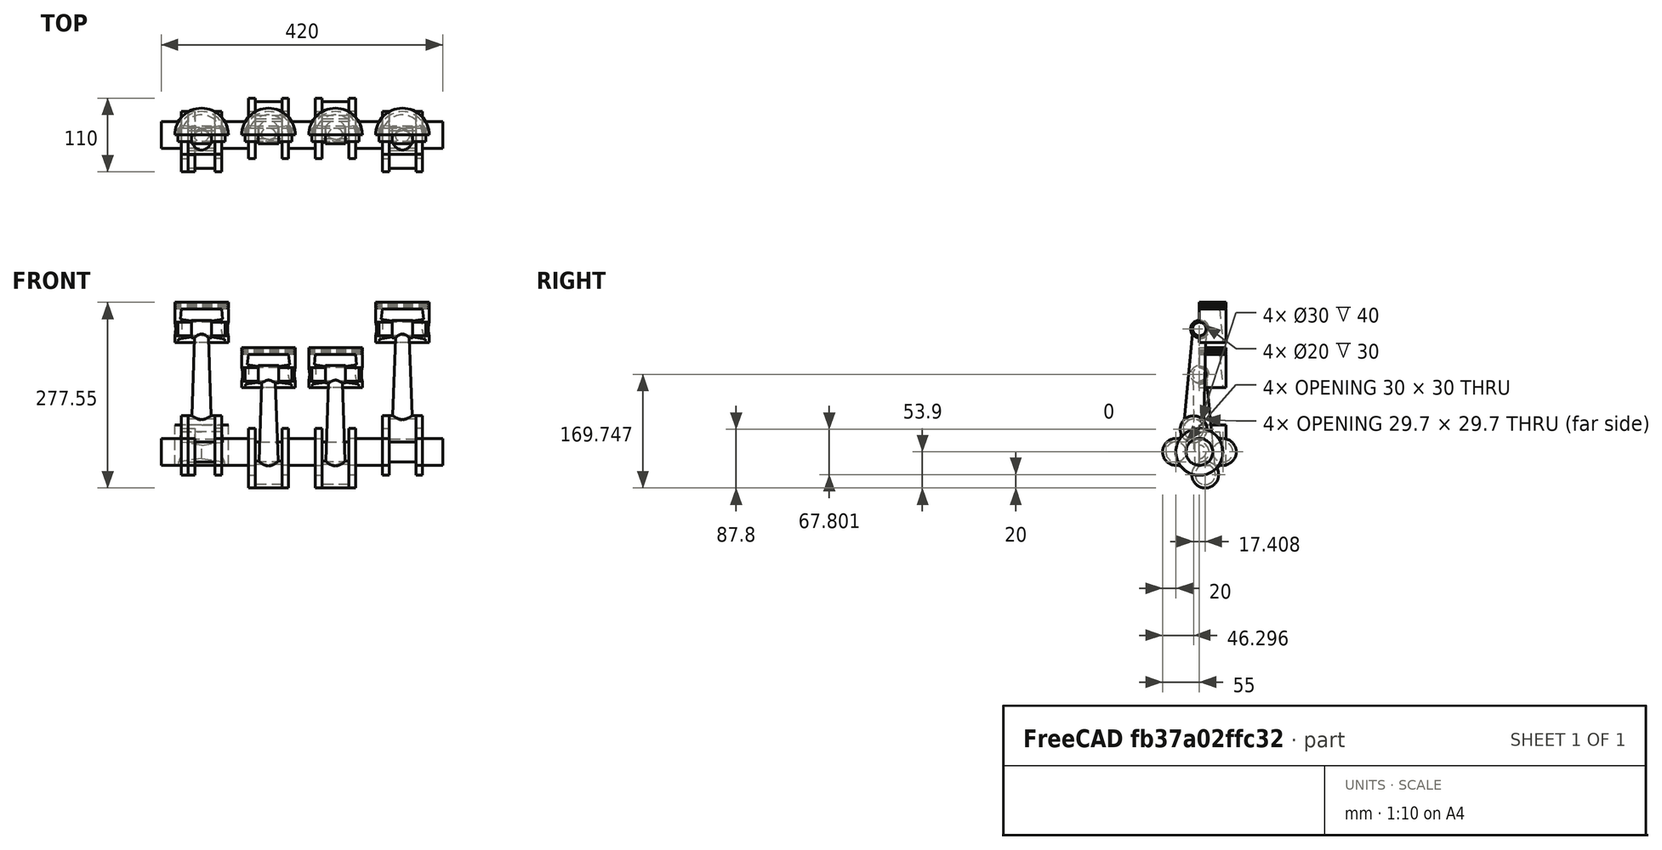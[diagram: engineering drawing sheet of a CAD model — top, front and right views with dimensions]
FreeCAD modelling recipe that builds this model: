
FCSTD DOCUMENT  (FreeCAD 0.18R16093 +53 (Git))
Label: 198 - ENGINE ANIMATION
License: All rights reserved
LicenseURL: http://en.wikipedia.org/wiki/All_rights_reserved
objects: Part::Cylinder×33, Part::Feature×20, Part::Cut×17, Part::Compound×12, App::DocumentObjectGroupPython×10, Part::MultiFuse×9, Part::Cone×6, Part::FeaturePython×4, Part::Fillet×1
note: 102 computed .brp shape members not serialized (recipe doc carries the construction recipe); baked Part::Feature solids carry a one-line shape summary decoded from their .brp

FEATURE [Part::Cylinder] Cylinder
  Angle = 180
  AttacherType = Attacher::AttachEngine3D
  Height = 60
  Placement = pos=(0,0,-20) rot=(0,0,1;0rad)
  Radius = 40
FEATURE [Part::Cone] Cone
  Angle = 360
  AttacherType = Attacher::AttachEngine3D
  Height = 50
  Placement = pos=(0,0,-20) rot=(0,0,1;0rad)
  Radius1 = 35
  Radius2 = 30
FEATURE [Part::Cut] Cut
  Base = -> Cylinder
  Tool = -> Cone
FEATURE [Part::Cone] Cone001
  Angle = 180
  AttacherType = Attacher::AttachEngine3D
  Height = 35
  Placement = pos=(0,0,0) rot=(0,-1,0;1.5708rad)
  Radius1 = 10
  Radius2 = 15
FEATURE [Part::Feature] Cone001001  label="Cone002"
  Placement = pos=(0,0,0) rot=(0,1,0;1.5708rad)
  shape: bbox 35 x 15 x 30 mm, 5 faces (baked)
FEATURE [Part::MultiFuse] Fusion
  Shapes = -> [Cone001001,Cone001,Cut]
FEATURE [Part::Feature] Fusion001
  shape: bbox 80 x 40 x 60 mm, 8 faces (baked)
FEATURE [Part::Cylinder] Cylinder001
  Angle = 360
  AttacherType = Attacher::AttachEngine3D
  Height = 100
  Placement = pos=(50,0,1.1e-14) rot=(0,-1,0;1.5708rad)
  Radius = 10
FEATURE [Part::Cut] Cut001
  Base = -> Fusion001
  Tool = -> Cylinder001
FEATURE [Part::Cylinder] Cylinder002
  Angle = 360
  AttacherType = Attacher::AttachEngine3D
  Height = 30
  Placement = pos=(15,0,3e-15) rot=(0,-1,0;1.5708rad)
  Radius = 13
FEATURE [Part::Cut] Cut002
  Base = -> Cut001
  Tool = -> Cylinder002
FEATURE [Part::FeaturePython] Tube  # WARN: FeaturePython — macro-defined, semantics opaque (R4)
  Height = 1
  InnerRadius = 39
  OuterRadius = 41
  Placement = pos=(0,0,36) rot=(0,0,1;0rad)
FEATURE [Part::Feature] Tube001
  Placement = pos=(0,0,33) rot=(0,0,1;0rad)
  shape: bbox 82 x 82 x 1 mm, 4 faces (baked)
FEATURE [Part::Feature] Tube002
  Placement = pos=(0,0,30) rot=(0,0,1;0rad)
  shape: bbox 82 x 82 x 1 mm, 4 faces (baked)
FEATURE [Part::Compound] Compound
  Links = -> [Tube002,Tube001,Tube]
FEATURE [Part::Cut] Cut003
  Base = -> Cut002
  Tool = -> Compound
FEATURE [Part::Cylinder] Cylinder003
  Angle = 360
  AttacherType = Attacher::AttachEngine3D
  Height = 70
  Placement = pos=(35,0,8e-15) rot=(0,-1,0;1.5708rad)
  Radius = 10
FEATURE [Part::Compound] Compound001  label="PISTON"
  Links = -> [Cylinder003,Cut003]
  Placement = pos=(0,0,183.648) rot=(0,0,1;0rad)
FEATURE [Part::Cylinder] Cylinder004
  Angle = 360
  AttacherType = Attacher::AttachEngine3D
  Height = 30
  Placement = pos=(15,0,150) rot=(0,-1,0;1.5708rad)
  Radius = 13
FEATURE [Part::Cone] Cone001002  label="Cone003"
  Angle = 360
  AttacherType = Attacher::AttachEngine3D
  Height = 150
  Radius1 = 15
  Radius2 = 10
FEATURE [Part::Cylinder] Cylinder005
  Angle = 360
  AttacherType = Attacher::AttachEngine3D
  Height = 40
  Placement = pos=(20,0,4e-15) rot=(0,-1,0;1.5708rad)
  Radius = 20
FEATURE [Part::MultiFuse] Fusion002
  Shapes = -> [Cylinder005,Cone001002,Cylinder004]
FEATURE [Part::Cylinder] Cylinder006
  Angle = 360
  AttacherType = Attacher::AttachEngine3D
  Height = 100
  Placement = pos=(50,0,150) rot=(0,-1,0;1.5708rad)
  Radius = 10
FEATURE [Part::Cylinder] Cylinder007
  Angle = 360
  AttacherType = Attacher::AttachEngine3D
  Height = 100
  Placement = pos=(50,0,1.1e-14) rot=(0,-1,0;1.5708rad)
  Radius = 15
FEATURE [Part::Compound] Compound002
  Links = -> [Cylinder007,Cylinder006]
FEATURE [Part::Cut] Cut004  label="CRANK"
  Base = -> Fusion002
  Placement = pos=(0,-8.70415,33.9004) rot=(1,0,0;6.22513rad)
  Tool = -> Compound002
FEATURE [Part::Cylinder] Cylinder008
  Angle = 360
  AttacherType = Attacher::AttachEngine3D
  Height = 10
  Placement = pos=(-20,-35,-4e-15) rot=(0,1,0;1.5708rad)
  Radius = 20
FEATURE [Part::Cylinder] Cylinder009
  Angle = 360
  AttacherType = Attacher::AttachEngine3D
  Height = 10
  Placement = pos=(-20,0,-4e-15) rot=(0,1,0;1.5708rad)
  Radius = 35
FEATURE [Part::MultiFuse] Fusion003
  Shapes = -> [Cylinder009,Cylinder008]
FEATURE [Part::Feature] Fusion003001  label="Fusion004"
  shape: bbox 10 x 90 x 70 mm, 4 faces (baked)
FEATURE [Part::Fillet] Fillet
  Base = -> Fusion003001
  Edges = 2 edges r=10: [Edge5,Edge8]
  Placement = pos=(-10,0,0) rot=(0,0,1;0rad)
FEATURE [Part::Cylinder] Cylinder010
  Angle = 360
  AttacherType = Attacher::AttachEngine3D
  Height = 40
  Placement = pos=(-20,-35,-4e-15) rot=(0,1,0;1.5708rad)
  Radius = 15
FEATURE [Part::Cylinder] Cylinder011
  Angle = 360
  AttacherType = Attacher::AttachEngine3D
  Height = 30
  Placement = pos=(-30,0,-7e-15) rot=(0,-1,0;1.5708rad)
  Radius = 20
FEATURE [Part::MultiFuse] Fusion003002  label="CRANKSHAFT"
  Shapes = -> [Cylinder011,Cylinder010,Fillet]
FEATURE [App::DocumentObjectGroupPython] My_Placer001  # scripted group (container) (typed FeaturePython)
  Placement = pos=(0,0,183.648) rot=(0,0,1;0rad)
  RotAxis = (0,0,1)
  RotCenter = (0,0,0)
  arc = 0
  arc0 = 0
  arc1 = 90
  target = -> Compound001
  time = 0.21
  x = 0
  x0 = 0.24869
  x1 = 0.968583
  y = 0
  y0 = 0.0580276
  y1 = 0.0580603
  z = 150*z1+35*x1
  z0 = 3.32661
  z1 = 0.998315
  expr: z1 = cos(z0)
  expr: z0 = y1 * 180 / pi
  expr: y1 = y0 + 1 / 2 * y0 ^ 3 / 3 + 3 / 8 * y0 ^ 5 / 5 + 15 / 48 * y0 ^ 7 / 7
  expr: y0 = x0 * 35 / 150
  expr: x1 = sin(time * 360)
  expr: x0 = cos(time * 360)
FEATURE [App::DocumentObjectGroupPython] My_Placer002  # scripted group (container) (typed FeaturePython)
  Placement = pos=(0,-8.70415,33.9004) rot=(1,0,0;-0.05806rad)
  RotAxis = (1,0,0)
  RotCenter = (0,0,0)
  arc =  -z0
  arc0 = 0
  arc1 = 90
  target = -> Cut004
  time = 0.21
  x = 0
  x0 = 0.24869
  x1 = 0.968583
  y = -35*x0
  y0 = 0.0580276
  y1 = 0.0580603
  z = 35*x1
  z0 = 3.32661
  z1 = 0.998315
  expr: z1 = cos(z0)
  expr: z0 = y1 * 180 / pi
  expr: y1 = y0 + 1 / 2 * y0 ^ 3 / 3 + 3 / 8 * y0 ^ 5 / 5 + 15 / 48 * y0 ^ 7 / 7
  expr: y0 = x0 * 35 / 150
  expr: x1 = sin(time * 360)
  expr: x0 = cos(time * 360)
FEATURE [Part::Feature] Fusion003002001  label="CRANKSHAFT001"
  shape: bbox 80 x 90 x 70 mm, 10 faces (baked)
FEATURE [Part::Feature] Fusion003002002  label="CRANKSHAFT002"
  Placement = pos=(0,0,0) rot=(0,1,0;3.14159rad)
  shape: bbox 80 x 90 x 70 mm, 10 faces (baked)
FEATURE [Part::MultiFuse] Fusion003002003
  Shapes = -> [Fusion003002002,Fusion003002001]
FEATURE [Part::Feature] Fusion003002003001  label="Fusion003002004"
  Placement = pos=(100,0,0) rot=(1,0,0;3.14159rad)
  shape: bbox 120 x 90 x 70 mm, 18 faces (baked)
FEATURE [Part::Feature] Fusion003002003002  label="Fusion003002005"
  Placement = pos=(200,0,0) rot=(1,0,0;3.14159rad)
  shape: bbox 120 x 90 x 70 mm, 18 faces (baked)
FEATURE [Part::Feature] Fusion003002003003  label="Fusion003002006"
  Placement = pos=(300,0,0) rot=(0,0,1;0rad)
  shape: bbox 120 x 90 x 70 mm, 18 faces (baked)
FEATURE [Part::MultiFuse] Fusion003002003004
  Shapes = -> [Fusion003002003003,Fusion003002003002,Fusion003002003001,Fusion003002003]
FEATURE [Part::Feature] Fusion003002003004001  label="CRANKSHAFT003"
  Placement = pos=(0,0,0) rot=(1,0,0;4.96372rad)
  shape: bbox 420 x 70 x 107.8 mm, 59 faces (baked)
FEATURE [App::DocumentObjectGroupPython] My_Placer  # scripted group (container) (typed FeaturePython)
  Placement = pos=(0,0,0) rot=(1,0,0;-1.31947rad)
  RotAxis = (1,0,0)
  RotCenter = (0,0,0)
  arc = -time*360
  arc0 = 0
  arc1 = 90
  target = -> Fusion003002003004001
  time = 0.21
  x = 0
  x0 = 0
  x1 = 200
  y = 0
  y0 = 0
  y1 = 0
  z = 0
  z0 = 0
  z1 = 0
FEATURE [Part::Feature] Tube003
  Placement = pos=(0,0,33) rot=(0,0,1;0rad)
  shape: bbox 82 x 82 x 1 mm, 4 faces (baked)
FEATURE [Part::Feature] Tube004
  Placement = pos=(0,0,30) rot=(0,0,1;0rad)
  shape: bbox 82 x 82 x 1 mm, 4 faces (baked)
FEATURE [Part::Cylinder] Cylinder012
  Angle = 360
  AttacherType = Attacher::AttachEngine3D
  Height = 100
  Placement = pos=(50,0,1.1e-14) rot=(0,-1,0;1.5708rad)
  Radius = 10
FEATURE [Part::Cylinder] Cylinder013
  Angle = 360
  AttacherType = Attacher::AttachEngine3D
  Height = 30
  Placement = pos=(15,0,3e-15) rot=(0,-1,0;1.5708rad)
  Radius = 13
FEATURE [Part::Feature] Fusion003002003004002
  shape: bbox 80 x 40 x 60 mm, 8 faces (baked)
FEATURE [Part::Cut] Cut007
  Base = -> Fusion003002003004002
  Tool = -> Cylinder012
FEATURE [Part::Cut] Cut005
  Base = -> Cut007
  Tool = -> Cylinder013
FEATURE [Part::Cylinder] Cylinder014
  Angle = 360
  AttacherType = Attacher::AttachEngine3D
  Height = 70
  Placement = pos=(35,0,8e-15) rot=(0,-1,0;1.5708rad)
  Radius = 10
FEATURE [Part::FeaturePython] Tube005  # WARN: FeaturePython — macro-defined, semantics opaque (R4)
  Height = 1
  InnerRadius = 39
  OuterRadius = 41
  Placement = pos=(0,0,36) rot=(0,0,1;0rad)
FEATURE [Part::Compound] Compound003
  Links = -> [Tube004,Tube003,Tube005]
FEATURE [Part::Cut] Cut006
  Base = -> Cut005
  Tool = -> Compound003
FEATURE [Part::Compound] Compound004  label="PISTON001"
  Links = -> [Cylinder014,Cut006]
  Placement = pos=(100,0,115.847) rot=(0,0,1;0rad)
FEATURE [App::DocumentObjectGroupPython] My_Placer003  # scripted group (container) (typed FeaturePython)
  Placement = pos=(100,0,115.847) rot=(0,0,1;0rad)
  RotAxis = (0,0,1)
  RotCenter = (0,0,0)
  arc = 0
  arc0 = 0
  arc1 = 90
  target = -> Compound004
  time = 0.21
  x = 100
  x0 = 0.24869
  x1 = 0.968583
  y = 0
  y0 = 0.0580276
  y1 = 0.0580603
  z = 150*z1-35*x1
  z0 = 3.32661
  z1 = 0.998315
  expr: z1 = cos(z0)
  expr: z0 = y1 * 180 / pi
  expr: y1 = y0 + 1 / 2 * y0 ^ 3 / 3 + 3 / 8 * y0 ^ 5 / 5 + 15 / 48 * y0 ^ 7 / 7
  expr: y0 = x0 * 35 / 150
  expr: x1 = sin(time * 360)
  expr: x0 = cos(time * 360)
FEATURE [Part::Feature] Tube006
  Placement = pos=(0,0,33) rot=(0,0,1;0rad)
  shape: bbox 82 x 82 x 1 mm, 4 faces (baked)
FEATURE [Part::Feature] Tube007
  Placement = pos=(0,0,30) rot=(0,0,1;0rad)
  shape: bbox 82 x 82 x 1 mm, 4 faces (baked)
FEATURE [Part::Cylinder] Cylinder015
  Angle = 360
  AttacherType = Attacher::AttachEngine3D
  Height = 100
  Placement = pos=(50,0,1.1e-14) rot=(0,-1,0;1.5708rad)
  Radius = 10
FEATURE [Part::Cylinder] Cylinder016
  Angle = 360
  AttacherType = Attacher::AttachEngine3D
  Height = 30
  Placement = pos=(15,0,3e-15) rot=(0,-1,0;1.5708rad)
  Radius = 13
FEATURE [Part::Feature] Fusion003002003004003
  shape: bbox 80 x 40 x 60 mm, 8 faces (baked)
FEATURE [Part::Cut] Cut010
  Base = -> Fusion003002003004003
  Tool = -> Cylinder015
FEATURE [Part::Cut] Cut008
  Base = -> Cut010
  Tool = -> Cylinder016
FEATURE [Part::Cylinder] Cylinder017
  Angle = 360
  AttacherType = Attacher::AttachEngine3D
  Height = 70
  Placement = pos=(35,0,8e-15) rot=(0,-1,0;1.5708rad)
  Radius = 10
FEATURE [Part::FeaturePython] Tube008  # WARN: FeaturePython — macro-defined, semantics opaque (R4)
  Height = 1
  InnerRadius = 39
  OuterRadius = 41
  Placement = pos=(0,0,36) rot=(0,0,1;0rad)
FEATURE [Part::Compound] Compound005
  Links = -> [Tube007,Tube006,Tube008]
FEATURE [Part::Cut] Cut009
  Base = -> Cut008
  Tool = -> Compound005
FEATURE [Part::Compound] Compound006  label="PISTON002"
  Links = -> [Cylinder017,Cut009]
  Placement = pos=(200,0,115.847) rot=(0,0,1;0rad)
FEATURE [App::DocumentObjectGroupPython] My_Placer004  # scripted group (container) (typed FeaturePython)
  Placement = pos=(200,0,115.847) rot=(0,0,1;0rad)
  RotAxis = (0,0,1)
  RotCenter = (0,0,0)
  arc = 0
  arc0 = 0
  arc1 = 90
  target = -> Compound006
  time = 0.21
  x = 200
  x0 = 0.24869
  x1 = 0.968583
  y = 0
  y0 = 0.0580276
  y1 = 0.0580603
  z = 150*z1-35*x1
  z0 = 3.32661
  z1 = 0.998315
  expr: z1 = cos(z0)
  expr: z0 = y1 * 180 / pi
  expr: y1 = y0 + 1 / 2 * y0 ^ 3 / 3 + 3 / 8 * y0 ^ 5 / 5 + 15 / 48 * y0 ^ 7 / 7
  expr: y0 = x0 * 35 / 150
  expr: x1 = sin(time * 360)
  expr: x0 = cos(time * 360)
FEATURE [Part::Feature] Tube009
  Placement = pos=(0,0,33) rot=(0,0,1;0rad)
  shape: bbox 82 x 82 x 1 mm, 4 faces (baked)
FEATURE [Part::Feature] Tube010
  Placement = pos=(0,0,30) rot=(0,0,1;0rad)
  shape: bbox 82 x 82 x 1 mm, 4 faces (baked)
FEATURE [Part::Cylinder] Cylinder018
  Angle = 360
  AttacherType = Attacher::AttachEngine3D
  Height = 100
  Placement = pos=(50,0,1.1e-14) rot=(0,-1,0;1.5708rad)
  Radius = 10
FEATURE [Part::Cylinder] Cylinder019
  Angle = 360
  AttacherType = Attacher::AttachEngine3D
  Height = 30
  Placement = pos=(15,0,3e-15) rot=(0,-1,0;1.5708rad)
  Radius = 13
FEATURE [Part::Feature] Fusion003002003004004
  shape: bbox 80 x 40 x 60 mm, 8 faces (baked)
FEATURE [Part::Cut] Cut013
  Base = -> Fusion003002003004004
  Tool = -> Cylinder018
FEATURE [Part::Cut] Cut011
  Base = -> Cut013
  Tool = -> Cylinder019
FEATURE [Part::Cylinder] Cylinder020
  Angle = 360
  AttacherType = Attacher::AttachEngine3D
  Height = 70
  Placement = pos=(35,0,8e-15) rot=(0,-1,0;1.5708rad)
  Radius = 10
FEATURE [Part::FeaturePython] Tube011  # WARN: FeaturePython — macro-defined, semantics opaque (R4)
  Height = 1
  InnerRadius = 39
  OuterRadius = 41
  Placement = pos=(0,0,36) rot=(0,0,1;0rad)
FEATURE [Part::Compound] Compound007
  Links = -> [Tube010,Tube009,Tube011]
FEATURE [Part::Cut] Cut012
  Base = -> Cut011
  Tool = -> Compound007
FEATURE [Part::Compound] Compound008  label="PISTON003"
  Links = -> [Cylinder020,Cut012]
  Placement = pos=(300,0,183.648) rot=(0,0,1;0rad)
FEATURE [App::DocumentObjectGroupPython] My_Placer005  # scripted group (container) (typed FeaturePython)
  Placement = pos=(300,0,183.648) rot=(0,0,1;0rad)
  RotAxis = (0,0,1)
  RotCenter = (0,0,0)
  arc = 0
  arc0 = 0
  arc1 = 90
  target = -> Compound008
  time = 0.21
  x = 300
  x0 = 0.24869
  x1 = 0.968583
  y = 0
  y0 = 0.0580276
  y1 = 0.0580603
  z = 150*z1+35*x1
  z0 = 3.32661
  z1 = 0.998315
  expr: z1 = cos(z0)
  expr: z0 = y1 * 180 / pi
  expr: y1 = y0 + 1 / 2 * y0 ^ 3 / 3 + 3 / 8 * y0 ^ 5 / 5 + 15 / 48 * y0 ^ 7 / 7
  expr: y0 = x0 * 35 / 150
  expr: x1 = sin(time * 360)
  expr: x0 = cos(time * 360)
FEATURE [Part::Cylinder] Cylinder021
  Angle = 360
  AttacherType = Attacher::AttachEngine3D
  Height = 40
  Placement = pos=(20,0,4e-15) rot=(0,-1,0;1.5708rad)
  Radius = 20
FEATURE [Part::Cylinder] Cylinder022
  Angle = 360
  AttacherType = Attacher::AttachEngine3D
  Height = 30
  Placement = pos=(15,0,150) rot=(0,-1,0;1.5708rad)
  Radius = 13
FEATURE [Part::Cylinder] Cylinder023
  Angle = 360
  AttacherType = Attacher::AttachEngine3D
  Height = 100
  Placement = pos=(50,0,150) rot=(0,-1,0;1.5708rad)
  Radius = 10
FEATURE [Part::Cylinder] Cylinder024
  Angle = 360
  AttacherType = Attacher::AttachEngine3D
  Height = 100
  Placement = pos=(50,0,1.1e-14) rot=(0,-1,0;1.5708rad)
  Radius = 15
FEATURE [Part::Compound] Compound009
  Links = -> [Cylinder024,Cylinder023]
FEATURE [Part::Cone] Cone001003  label="Cone004"
  Angle = 360
  AttacherType = Attacher::AttachEngine3D
  Height = 150
  Radius1 = 15
  Radius2 = 10
FEATURE [Part::MultiFuse] Fusion003002003004005
  Shapes = -> [Cylinder021,Cone001003,Cylinder022]
FEATURE [Part::Cut] Cut014  label="CRANK001"
  Base = -> Fusion003002003004005
  Placement = pos=(300,-8.70415,33.9004) rot=(1,0,0;6.22513rad)
  Tool = -> Compound009
FEATURE [App::DocumentObjectGroupPython] My_Placer006  # scripted group (container) (typed FeaturePython)
  Placement = pos=(300,-8.70415,33.9004) rot=(1,0,0;-0.05806rad)
  RotAxis = (1,0,0)
  RotCenter = (0,0,0)
  arc =  -z0
  arc0 = 0
  arc1 = 90
  target = -> Cut014
  time = 0.21
  x = 300
  x0 = 0.24869
  x1 = 0.968583
  y = -35*x0
  y0 = 0.0580276
  y1 = 0.0580603
  z = 35*x1
  z0 = 3.32661
  z1 = 0.998315
  expr: z1 = cos(z0)
  expr: z0 = y1 * 180 / pi
  expr: y1 = y0 + 1 / 2 * y0 ^ 3 / 3 + 3 / 8 * y0 ^ 5 / 5 + 15 / 48 * y0 ^ 7 / 7
  expr: y0 = x0 * 35 / 150
  expr: x1 = sin(time * 360)
  expr: x0 = cos(time * 360)
FEATURE [Part::Cylinder] Cylinder025
  Angle = 360
  AttacherType = Attacher::AttachEngine3D
  Height = 40
  Placement = pos=(20,0,4e-15) rot=(0,-1,0;1.5708rad)
  Radius = 20
FEATURE [Part::Cylinder] Cylinder026
  Angle = 360
  AttacherType = Attacher::AttachEngine3D
  Height = 30
  Placement = pos=(15,0,150) rot=(0,-1,0;1.5708rad)
  Radius = 13
FEATURE [Part::Cylinder] Cylinder027
  Angle = 360
  AttacherType = Attacher::AttachEngine3D
  Height = 100
  Placement = pos=(50,0,150) rot=(0,-1,0;1.5708rad)
  Radius = 10
FEATURE [Part::Cylinder] Cylinder028
  Angle = 360
  AttacherType = Attacher::AttachEngine3D
  Height = 100
  Placement = pos=(50,0,1.1e-14) rot=(0,-1,0;1.5708rad)
  Radius = 15
FEATURE [Part::Compound] Compound010
  Links = -> [Cylinder028,Cylinder027]
FEATURE [Part::Cone] Cone001004  label="Cone005"
  Angle = 360
  AttacherType = Attacher::AttachEngine3D
  Height = 150
  Radius1 = 15
  Radius2 = 10
FEATURE [Part::MultiFuse] Fusion003002003004006
  Shapes = -> [Cylinder025,Cone001004,Cylinder026]
FEATURE [Part::Cut] Cut015  label="CRANK002"
  Base = -> Fusion003002003004006
  Placement = pos=(200,8.70415,-33.9004) rot=(1,0,0;0.05806rad)
  Tool = -> Compound010
FEATURE [App::DocumentObjectGroupPython] My_Placer007  # scripted group (container) (typed FeaturePython)
  Placement = pos=(200,8.70415,-33.9004) rot=(1,0,0;0.05806rad)
  RotAxis = (1,0,0)
  RotCenter = (0,0,0)
  arc =  z0
  arc0 = 0
  arc1 = 90
  target = -> Cut015
  time = 0.21
  x = 200
  x0 = 0.24869
  x1 = 0.968583
  y = 35*x0
  y0 = 0.0580276
  y1 = 0.0580603
  z = -35*x1
  z0 = 3.32661
  z1 = 0.998315
  expr: z1 = cos(z0)
  expr: z0 = y1 * 180 / pi
  expr: y1 = y0 + 1 / 2 * y0 ^ 3 / 3 + 3 / 8 * y0 ^ 5 / 5 + 15 / 48 * y0 ^ 7 / 7
  expr: y0 = x0 * 35 / 150
  expr: x1 = sin(time * 360)
  expr: x0 = cos(time * 360)
FEATURE [Part::Cylinder] Cylinder029
  Angle = 360
  AttacherType = Attacher::AttachEngine3D
  Height = 40
  Placement = pos=(20,0,4e-15) rot=(0,-1,0;1.5708rad)
  Radius = 20
FEATURE [Part::Cylinder] Cylinder030
  Angle = 360
  AttacherType = Attacher::AttachEngine3D
  Height = 30
  Placement = pos=(15,0,150) rot=(0,-1,0;1.5708rad)
  Radius = 13
FEATURE [Part::Cylinder] Cylinder031
  Angle = 360
  AttacherType = Attacher::AttachEngine3D
  Height = 100
  Placement = pos=(50,0,150) rot=(0,-1,0;1.5708rad)
  Radius = 10
FEATURE [Part::Cylinder] Cylinder032
  Angle = 360
  AttacherType = Attacher::AttachEngine3D
  Height = 100
  Placement = pos=(50,0,1.1e-14) rot=(0,-1,0;1.5708rad)
  Radius = 15
FEATURE [Part::Compound] Compound011
  Links = -> [Cylinder032,Cylinder031]
FEATURE [Part::Cone] Cone001005  label="Cone006"
  Angle = 360
  AttacherType = Attacher::AttachEngine3D
  Height = 150
  Radius1 = 15
  Radius2 = 10
FEATURE [Part::MultiFuse] Fusion003002003004007
  Shapes = -> [Cylinder029,Cone001005,Cylinder030]
FEATURE [Part::Cut] Cut016  label="CRANK003"
  Base = -> Fusion003002003004007
  Placement = pos=(100,8.70415,-33.9004) rot=(1,0,0;0.05806rad)
  Tool = -> Compound011
FEATURE [App::DocumentObjectGroupPython] My_Placer008  # scripted group (container) (typed FeaturePython)
  Placement = pos=(100,8.70415,-33.9004) rot=(1,0,0;0.05806rad)
  RotAxis = (1,0,0)
  RotCenter = (0,0,0)
  arc =  z0
  arc0 = 0
  arc1 = 90
  target = -> Cut016
  time = 0.21
  x = 100
  x0 = 0.24869
  x1 = 0.968583
  y = 35*x0
  y0 = 0.0580276
  y1 = 0.0580603
  z = -35*x1
  z0 = 3.32661
  z1 = 0.998315
  expr: z1 = cos(z0)
  expr: z0 = y1 * 180 / pi
  expr: y1 = y0 + 1 / 2 * y0 ^ 3 / 3 + 3 / 8 * y0 ^ 5 / 5 + 15 / 48 * y0 ^ 7 / 7
  expr: y0 = x0 * 35 / 150
  expr: x1 = sin(time * 360)
  expr: x0 = cos(time * 360)
FEATURE [App::DocumentObjectGroupPython] My_Manager  # scripted group (container) (typed FeaturePython)
  Group = -> [My_Placer,My_Placer001,My_Placer002,My_Placer003,My_Placer004,My_Placer005,My_Placer006,My_Placer007,My_Placer008]
  intervall = 1000
  sleeptime = 0.02
  start = 0
  step = 21
  text = NO
